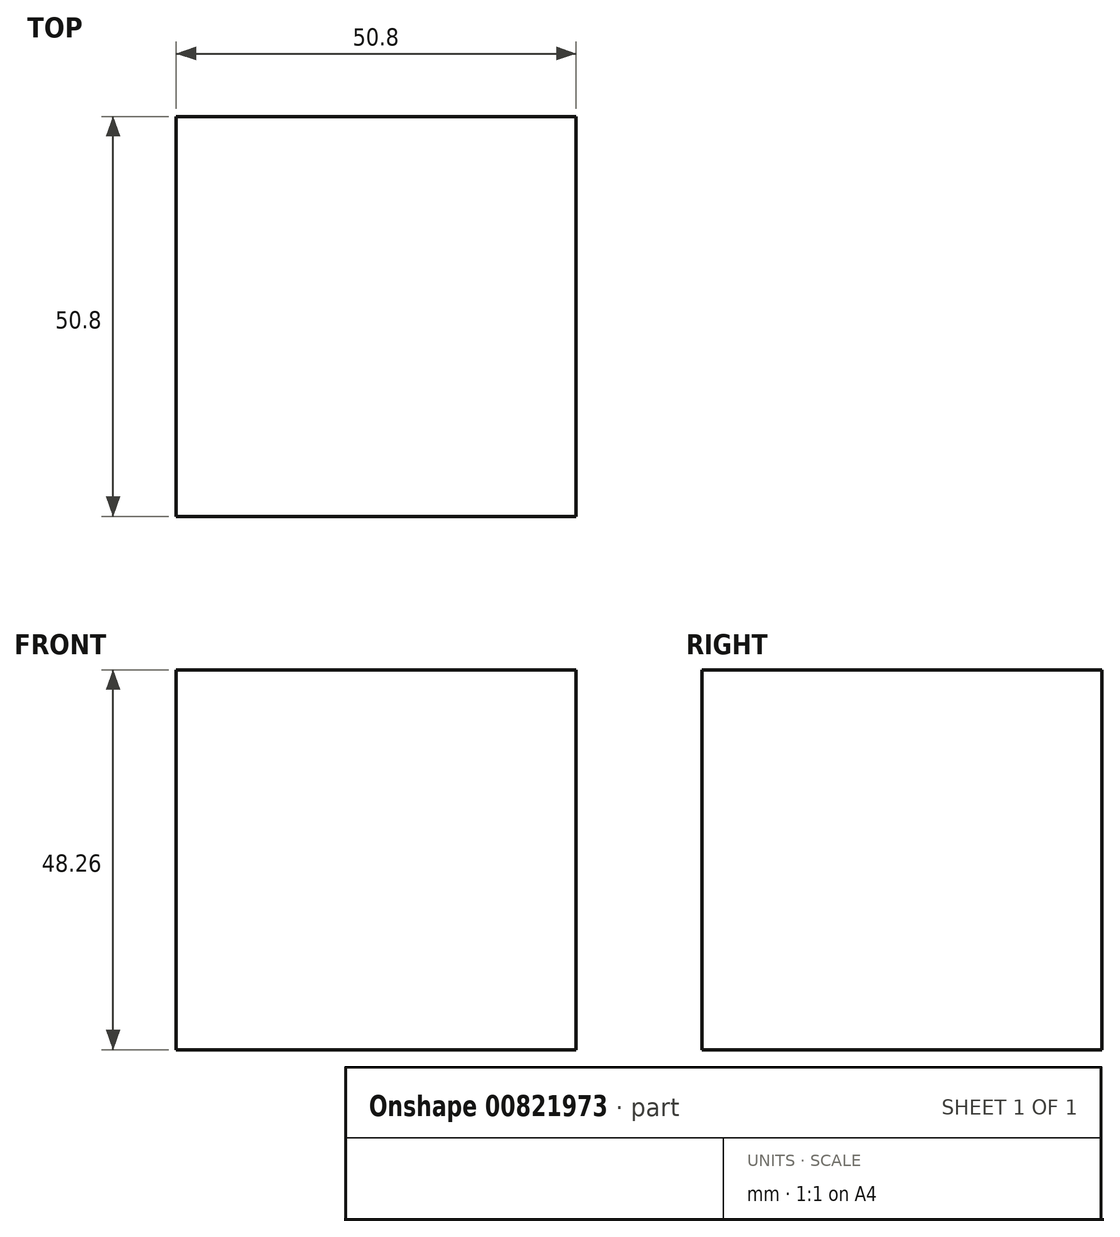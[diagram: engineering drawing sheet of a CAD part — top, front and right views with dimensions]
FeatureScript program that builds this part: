
annotation { "Feature Type Name" : "Feature", "Feature Type Description" : "" }
export const myFeature = defineFeature(function(context is Context, id is Id, definition is map)
    precondition{}
    {
        {
            var Q0;
            Q0=qCreatedBy(makeId("Front.planeOp"),FACE);
            var sketch = newSketch(context, id + "F0", { "sketchPlane" : qUnion([Q0])});
            skLineSegment(sketch, "E0.bottom", {"start": v(-25.4, 24.13) * mm, "end": v(25.4, 24.13) * mm});
            skLineSegment(sketch, "E0.top", {"start": v(-25.4, -24.13) * mm, "end": v(25.4, -24.13) * mm});
            skLineSegment(sketch, "E0.left", {"start": v(-25.4, 24.13) * mm, "end": v(-25.4, -24.13) * mm});
            skLineSegment(sketch, "E0.right", {"start": v(25.4, 24.13) * mm, "end": v(25.4, -24.13) * mm});
            skPoint(sketch, "E0.middle", {"position": v(0, 0) * mm});
            skSolve(sketch);
        }
        {
            var Q0;
            Q0=makeQuery(id+"F0.imprint","IMPRINT",FACE,{"disambiguationData":[TD([[makeQuery(id+"F0.imprint","IMPRINT",EDGE,{"derivedFrom":sQuery(id+"F0.wireOp",EDGE,"E0.bottom")}),-1.0]])]});
            extrude(context, id + "F1", {"entities" : qUnion([Q0]), "depth" : 50.8 * mm, "offsetDistance" : 25.4 * mm});
        }
    });
